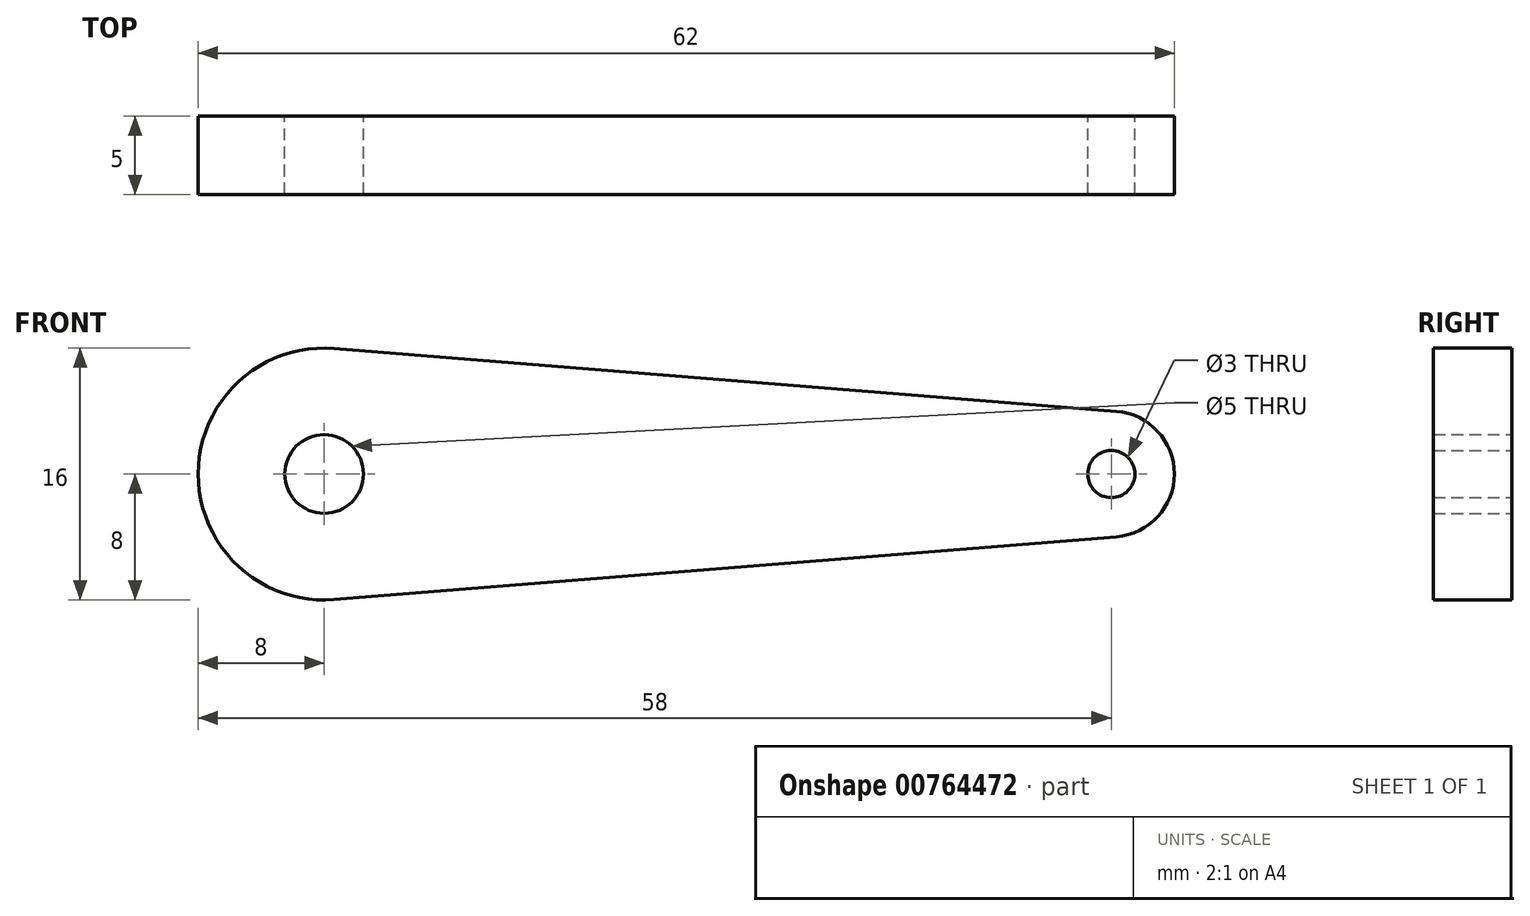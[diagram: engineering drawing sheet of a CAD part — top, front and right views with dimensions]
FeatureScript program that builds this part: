
annotation { "Feature Type Name" : "Feature", "Feature Type Description" : "" }
export const myFeature = defineFeature(function(context is Context, id is Id, definition is map)
    precondition{}
    {
        {
            var Q0;
            Q0=qCreatedBy(makeId("Front.planeOp"),FACE);
            var sketch = newSketch(context, id + "F0", { "sketchPlane" : qUnion([Q0])});
            skArc(sketch, "E0", {"start": v(0.64, 7.97) * mm, "mid": v(-8, 0) * mm, "end": v(0.64, -7.97) * mm});
            skLineSegment(sketch, "E1", {"start": v(0.64, -7.97) * mm, "end": v(50.32, -3.99) * mm});
            skArc(sketch, "E2", {"start": v(50.32, -3.99) * mm, "mid": v(54, 0) * mm, "end": v(50.32, 3.99) * mm});
            skLineSegment(sketch, "E3", {"start": v(0.64, 7.97) * mm, "end": v(50.32, 3.99) * mm});
            skCircle(sketch, "E4", {"center": v(50, 0) * mm, "radius": 1.5 * mm});
            skCircle(sketch, "E5", {"center": v(0, 0) * mm, "radius": 2.5 * mm});
            skSolve(sketch);
        }
        {
            var Q0;
            Q0=makeQuery(id+"F0.imprint","IMPRINT",FACE,{"disambiguationData":[TD([[makeQuery(id+"F0.imprint","IMPRINT",EDGE,{"derivedFrom":sQuery(id+"F0.wireOp",EDGE,"E0")}),1.0]])]});
            extrude(context, id + "F1", {"entities" : qUnion([Q0]), "depth" : 5 * mm, "offsetDistance" : 25 * mm});
        }
    });
